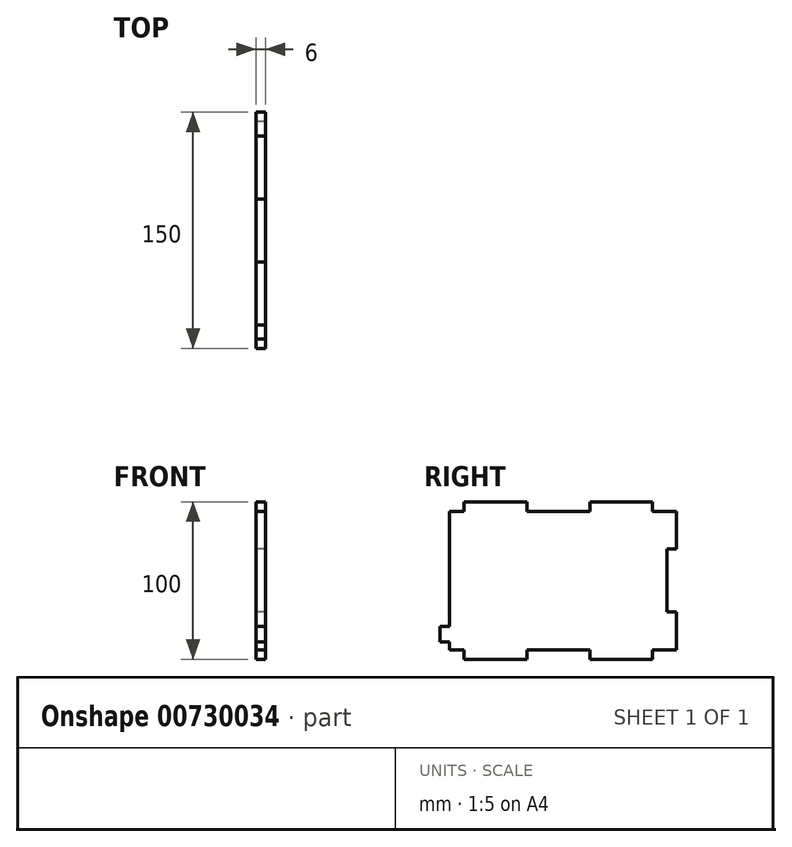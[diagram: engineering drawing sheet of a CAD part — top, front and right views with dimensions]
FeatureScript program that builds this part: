
annotation { "Feature Type Name" : "Feature", "Feature Type Description" : "" }
export const myFeature = defineFeature(function(context is Context, id is Id, definition is map)
    precondition{}
    {
        {
            var Q0;
            Q0=qCreatedBy(makeId("Right.planeOp"),FACE);
            var sketch = newSketch(context, id + "F0", { "sketchPlane" : qUnion([Q0])});
            skLineSegment(sketch, "E0", {"start": v(-50.5, 73) * mm, "end": v(-50.5, 79) * mm});
            skLineSegment(sketch, "E1", {"start": v(-50.5, 79) * mm, "end": v(-10.5, 79) * mm});
            skLineSegment(sketch, "E2", {"start": v(-10.5, 79) * mm, "end": v(-10.5, 73) * mm});
            skLineSegment(sketch, "E3", {"start": v(-10.5, 73) * mm, "end": v(29.5, 73) * mm});
            skLineSegment(sketch, "E4", {"start": v(29.5, 73) * mm, "end": v(29.5, 79) * mm});
            skLineSegment(sketch, "E5", {"start": v(29.5, 79) * mm, "end": v(69.5, 79) * mm});
            skLineSegment(sketch, "E6", {"start": v(69.5, 79) * mm, "end": v(69.5, 73) * mm});
            skLineSegment(sketch, "E7", {"start": v(69.5, 73) * mm, "end": v(84.5, 73) * mm});
            skLineSegment(sketch, "E8", {"start": v(84.5, 73) * mm, "end": v(84.5, 49) * mm});
            skLineSegment(sketch, "E9", {"start": v(84.5, 49) * mm, "end": v(78.5, 49) * mm});
            skLineSegment(sketch, "E10", {"start": v(78.5, 49) * mm, "end": v(78.5, 9) * mm});
            skLineSegment(sketch, "E11", {"start": v(78.5, 9) * mm, "end": v(84.5, 9) * mm});
            skLineSegment(sketch, "E12", {"start": v(84.5, 9) * mm, "end": v(84.5, -15) * mm});
            skLineSegment(sketch, "E13", {"start": v(84.5, -15) * mm, "end": v(69.5, -15) * mm});
            skLineSegment(sketch, "E14", {"start": v(69.5, -15) * mm, "end": v(69.5, -21) * mm});
            skLineSegment(sketch, "E15", {"start": v(69.5, -21) * mm, "end": v(29.5, -21) * mm});
            skLineSegment(sketch, "E16", {"start": v(29.5, -21) * mm, "end": v(29.5, -15) * mm});
            skLineSegment(sketch, "E17", {"start": v(29.5, -15) * mm, "end": v(-10.5, -15) * mm});
            skLineSegment(sketch, "E18", {"start": v(-10.5, -15) * mm, "end": v(-10.5, -21) * mm});
            skLineSegment(sketch, "E19", {"start": v(-10.5, -21) * mm, "end": v(-50.5, -21) * mm});
            skLineSegment(sketch, "E20", {"start": v(-50.5, -21) * mm, "end": v(-50.5, -15) * mm});
            skLineSegment(sketch, "E21", {"start": v(-50.5, -15) * mm, "end": v(-59.5, -15) * mm});
            skLineSegment(sketch, "E22", {"start": v(-59.5, -15) * mm, "end": v(-59.5, -10) * mm});
            skLineSegment(sketch, "E23", {"start": v(-59.5, -10) * mm, "end": v(-65.5, -10) * mm});
            skLineSegment(sketch, "E24", {"start": v(-65.5, -10) * mm, "end": v(-65.5, 0) * mm});
            skLineSegment(sketch, "E25", {"start": v(-65.5, 0) * mm, "end": v(-59.5, 0) * mm});
            skLineSegment(sketch, "E26", {"start": v(-50.5, 73) * mm, "end": v(-59.5, 73) * mm});
            skLineSegment(sketch, "E27", {"start": v(-59.5, 0) * mm, "end": v(-59.5, 73) * mm});
            skSolve(sketch);
        }
        {
            var Q0;
            Q0 = qSketchRegion(id + "F0", true);
            extrude(context, id + "F1", {"entities" : qUnion([Q0]), "depth" : 6 * mm, "offsetDistance" : 25 * mm});
        }
    });
